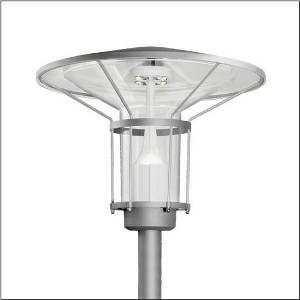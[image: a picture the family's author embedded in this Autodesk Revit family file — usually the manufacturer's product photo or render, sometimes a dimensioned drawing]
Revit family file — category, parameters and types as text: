
# Revit family: laterne_classic_iq___pl1_2s_5xa5245jf14h_d895
name_source: partatom
category: Lighting Fixtures
units: mm (PartAtom-declared; Revit-internal decimal feet)

## family parameters
Cut with Voids When Loaded = No
Host = Face
Light Source = No
Part Type = Normal
Room Calculation Point = No
Round Connector Dimension = Use Diameter
Shared = No

## types (1)
- --- (1 x LED, 2660 lm, 19.3 W, 3000K)
    Apparent Load = 19 VA
    CIE Flux Codes = 21 60 93 97 100
    Color Rendering = 70
    Color Temperature = 3000K
    Default Elevation = 1800 mm
    Description = Lantern Classic iQ, mast luminaire, Module 540 iQ-SR, primary light control with 3 zone facetted reflector, of plastic, silver coated, highly specular, structured, primary optical cover: cover, of PMMA, transparent, light distribution: PL1.2s, light emission: direct distribution, primary light characteristic: symmetric, installation type: post-top, LED, High Power LED, rated luminous flux: 2.670lm, luminous efficacy: 138lm/W, light colour: 730, colour temperature: 3000K, control gear: iQ Street-Remote, control: Auto-Match, Temp-Guard, Lumen-Switch, Night-Set, Smart-Wire, Light-Fading, Desk-Remote (wireless, voltage-free reading and setting of iQ features in the workshop via application-optimized NFC function/RFID function), optimised constant luminous flux control (CLO 2.0), Street-Remote, pre-setting: logarithmic dimming characteristic, with terminal, 6-pole, max. 2.5mm², mains connection: 230..240V, AC, 50/60Hz, start of lifetime: 19W, end of service life: 21W, reduction: 10W, luminaire housing, upper part, of glass-fibre reinforced polyester, coated, Siteco® metallic grey (DB 702S), diameter: 750mm, height: 596mm, spigot size: d x l = 76 x 70mm (post-top) | with reducer (optional accessory) 60 x 70mm, mounting height: 3..5m, post-top mast mounting element, of diecast aluminium, coated, Siteco® metallic grey (DB 702S), Module 540 iQ-SR, traffic white (RAL 9016), equipment: standard, protection rating (complete): IP65, insulation class (complete): insulation class II (safety insulation), certification: CE, ENEC, VDE, packaging unit: 1 piece

Light Distribution: PL1.2s
    Height = 596 mm
    Lamp = 1 x LED
    Lamp Light Flux = 2660 lm
    Lamp Power = 19.3 W
    Lamp count = 1
    Length = 750 mm
    Luminous efficacy = 138 lm/W
    Manufacturer = Siteco
    ModVariant = No
    Model = 5XA5245JF14H
    Number of Poles = 1
    OnlyDefault = Yes
    Power Factor = 1
    Product Name = Laterne Classic iQ | PL1.2s
    Product group = mast luminaire | pylon top
    ProductGroupID = 6100
    Protection Class = Protection class II
    Protection Degree = IP 65
    RLX_Detail_Level = 1
    RLX_Emergency_Light_Flux = 0 lm
    RLX_Emergency_Type = 0
    RLX_Emergency_Type_DB = No
    RlxData = <blob elided: 37781 chars, md5=73a36586>
    Socket = socket
    Standby Power = 0 W
    System Light Flux = 2660 lm
    System Power = 19 W
    Type Comments = factory setting: luminous flux: 100 % | dim-lin: 254 | 403 mA
    Type Image = l_1006052.jpg
    URL = http://relux.com
    VarID = @adj_167219
    Voltage = 0 V
    Weight = 0.00 kg
    Width = 0 mm  [stored 0 ft]

note: [stored X ft] marks values corroborated as IEEE doubles in the binary element streams (Revit-internal decimal feet)

## geometry (parser evidence)
native form markers: Blend x4, Sweep x9
no freeform markers — native parametric forms only
